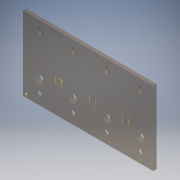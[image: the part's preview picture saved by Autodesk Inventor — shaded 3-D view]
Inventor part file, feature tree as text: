
AUTODESK INVENTOR PART (.ipt)
format: ipt  version: 2019 (Build 230136000, 136)  size: 166,400 bytes
history: native  units: in
note: dims shown in document units (in); Inventor stores cm internally (conversion verified against a paired STEP export)
features: reference x20, other x8, sketch x5, hole x3, projected_geometry x2, extrude x1
ambient origin geometry x8: Origin, YZ Plane, XZ Plane, XY Plane, X Axis, Y Axis, Z Axis, Center Point
bodies: Solid1 (feature_tree)
feature tree (39):
  extrude  "Extrusion1"  Depth=4.85in
  hole  "Hole1"  [1 undecoded]
  hole  "Hole2"  [1 undecoded]
  hole  "Hole3"  [1 undecoded]
  sketch  "Sketch5"  dims[d10=0.177in d11=0.75in d12=0.385in d13=0.25in d14=0.5635in d15=1.0in d16=0.8108in d19=0.177in d20=1.717in d21=0.332in d22=0.25in d23=0.5635in d24=1.0in d25=0.8108in d26=2.0in d27=0.177in d28=1.717in d29=0.332in d30=0.25in d31=0.5635in d32=1.0in d33=0.8108in d34=0.01in d35=0.01in]
  sketch  "Sketch1"  dims[d0=2.75in d1=4.85in]
  sketch  "Sketch2"  dims[d2=0.125in d3=0.0in d5=0.385in]
  sketch  "Sketch3"  dims[d6=0.6in d7=1.25in]
  projected_geometry  "Projected Loop1"
  sketch  "Sketch4"  dims[d8=1.25in d9=1.25in]
  projected_geometry  "Projected Loop2"
  reference  "Reference1"
  reference  "Reference2"
  reference  "Reference3"
  reference  "Reference4"
  reference  "Reference5"
  reference  "Reference6"
  reference  "Reference7"
  reference  "Reference8"
  reference  "Reference9"
  reference  "Reference10"
  reference  "Reference11"
  reference  "Reference12"
  reference  "Reference13"
  reference  "Reference14"
  reference  "Reference15"
  reference  "Reference16"
  reference  "Reference17"
  reference  "Reference18"
  reference  "Reference19"
  reference  "Reference20"
  parser-record x1  (decoder bookkeeping rows leaked as tree rows — omitted from the tree; the rows remain in map.json)
  other  "talon stack.iam"
  other  "Victor_SPX_217-9191:3"
  other  "217-9191-001 Rev3_1"
  other  "Victor_SPX_217-9191:4"
  other  "Victor_SPX_217-9191:2"
  other  "217-9191-002 Rev3_2"
  other  "Victor_SPX_217-9191:1"
note: 3 required parameter values undecoded (feature->parameter linkage not recoverable at this tier; creation-order binding heuristic only, values carry confidence <= 0.55)
note: 1 file-system path scrubbed to <path> (originals preserved in map.json)
